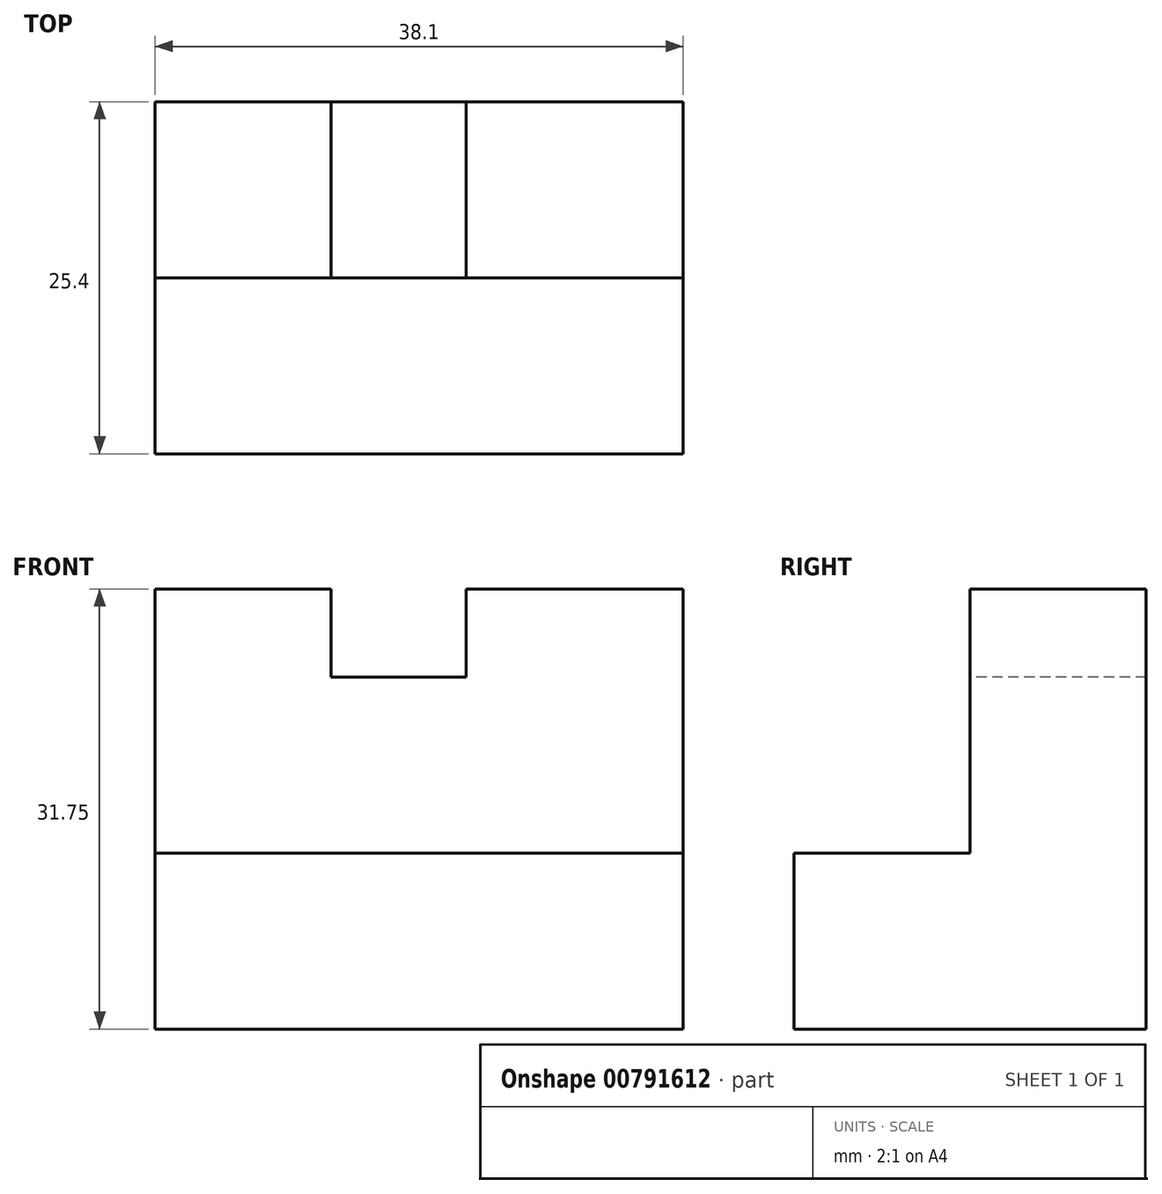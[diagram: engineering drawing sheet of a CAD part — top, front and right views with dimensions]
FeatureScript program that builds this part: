
annotation { "Feature Type Name" : "Feature", "Feature Type Description" : "" }
export const myFeature = defineFeature(function(context is Context, id is Id, definition is map)
    precondition{}
    {
        {
            var Q0;
            Q0=qCreatedBy(makeId("Front.planeOp"),FACE);
            var sketch = newSketch(context, id + "F0", { "sketchPlane" : qUnion([Q0])});
            skLineSegment(sketch, "E0", {"start": v(0, 0) * mm, "end": v(38.1, 0) * mm});
            skLineSegment(sketch, "E1", {"start": v(38.1, 0) * mm, "end": v(38.1, 31.75) * mm});
            skLineSegment(sketch, "E2", {"start": v(38.1, 31.75) * mm, "end": v(0, 31.75) * mm});
            skLineSegment(sketch, "E3", {"start": v(0, 31.75) * mm, "end": v(0, 0) * mm});
            skSolve(sketch);
        }
        {
            var Q0;
            Q0 = qSketchRegion(id + "F0", true);
            extrude(context, id + "F1", {"entities" : qUnion([Q0]), "depth" : 25.4 * mm, "offsetDistance" : 25.4 * mm});
        }
        {
            var Q0;
            Q0=makeQuery(id+"F1.opExtrude","SWEPT_FACE",FACE,{"disambiguationData":[OSD([sQuery(id+"F0.wireOp",EDGE,"E1")])]});
            var sketch = newSketch(context, id + "F2", { "sketchPlane" : qUnion([Q0])});
            skLineSegment(sketch, "E4", {"start": v(-25.4, 0) * mm, "end": v(-25.4, 12.7) * mm});
            skLineSegment(sketch, "E5", {"start": v(-25.4, 12.7) * mm, "end": v(-12.7, 12.7) * mm});
            skLineSegment(sketch, "E6", {"start": v(-12.7, 12.7) * mm, "end": v(-12.7, 31.75) * mm});
            skSolve(sketch);
        }
        {
            var Q0;
            Q0 = qSketchRegion(id + "F2", true);
            var Q1;
            {var subQ0=sQuery(id+"F2.wireOp",EDGE,"E5");Q1=makeQuery(id+"F2.imprint","IMPRINT",FACE,{"disambiguationData":[TD([[makeQuery(id+"F2.imprint","IMPRINT",EDGE,{"derivedFrom":subQ0}),1.0]])]});}
            extrude(context, id + "F3", {"entities" : qUnion([Q0, Q1]), "operationType" : NewBodyOperationType.REMOVE, "oppositeDirection" : true, "depth" : 38.1 * mm, "offsetDistance" : 25.4 * mm});
        }
        {
            var Q0;
            Q0=makeQuery(id+"F3.boolean.opBoolean","COPY",FACE,{"derivedFrom":makeQuery(id+"F3.opExtrude","SWEPT_FACE",FACE,{"disambiguationData":[OSD([sQuery(id+"F2.wireOp",EDGE,"E6")])]})});
            var sketch = newSketch(context, id + "F4", { "sketchPlane" : qUnion([Q0])});
            skLineSegment(sketch, "E7", {"start": v(0, 31.75) * mm, "end": v(12.7, 31.75) * mm});
            skLineSegment(sketch, "E8", {"start": v(12.7, 31.75) * mm, "end": v(12.7, 25.4) * mm});
            skLineSegment(sketch, "E9", {"start": v(12.7, 25.4) * mm, "end": v(22.44, 25.4) * mm});
            skLineSegment(sketch, "E10", {"start": v(22.44, 25.4) * mm, "end": v(22.44, 31.75) * mm});
            skLineSegment(sketch, "E11", {"start": v(22.44, 31.75) * mm, "end": v(38.1, 31.75) * mm});
            skSolve(sketch);
        }
        {
            var Q0;
            Q0 = qSketchRegion(id + "F4", true);
            var Q1;
            {var subQ0=sQuery(id+"F4.wireOp",EDGE,"E8");Q1=makeQuery(id+"F4.imprint","IMPRINT",FACE,{"disambiguationData":[TD([[makeQuery(id+"F4.imprint","IMPRINT",EDGE,{"derivedFrom":subQ0}),1.0]])]});}
            extrude(context, id + "F5", {"entities" : qUnion([Q0, Q1]), "operationType" : NewBodyOperationType.REMOVE, "oppositeDirection" : true, "depth" : 25.4 * mm, "offsetDistance" : 25.4 * mm});
        }
    });
